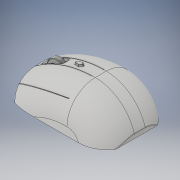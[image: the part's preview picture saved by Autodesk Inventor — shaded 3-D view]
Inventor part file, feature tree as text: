
AUTODESK INVENTOR PART (.ipt)
format: ipt  version: 2017 (Build 210142000, 142)  size: 1,075,200 bytes
history: native  units: in
note: dims shown in document units (in); Inventor stores cm internally (conversion verified against a paired STEP export)
features: sketch x12, extrude x7, other x6, fillet x5, sweep x2, mirror x1
ambient origin geometry x8: Origin, YZ Plane, XZ Plane, XY Plane, X Axis, Y Axis, Z Axis, Center Point
bodies: Solid1 (feature_tree)
feature tree (33):
  extrude  "main body"  Depth=0.1251in
  other  "middle of the mouse workplane"
  fillet  "curve the edges"  Radius=0.0409in
  other  "gap for mouse clicks"
  sweep  "gap made for mouse clicks"
  sweep  "gap for mouse clicks front"
  extrude  "far left gap for mouse clicks"  Depth=0.2314in TaperAngle=0.0deg
  mirror  "mirror mouse clicks for other side"
  extrude  "mouse wheel gap"  Depth=0.1974in
  extrude  "mouse wheel extion for proper width"  Depth=0.0053in
  fillet  "curve proper width for wheel gap"  [1 undecoded]
  other  "mouse wheel revolve plane"
  other  "wheel"
  extrude  "friction points"  Depth=0.0302in
  fillet  "wheel curve edge"  Radius=0.0046in
  other  "batter indicator workplane"
  extrude  "battery indicator cut out"  Depth=0.0199in TaperAngle=0.0deg
  extrude  "power indicator"  Depth=0.0687in
  fillet  "smooth the powe indicator"  Radius=0.0382in
  fillet  "Fillet6"  Radius=0.0043in
  sketch  "Sketch1"  dims[d0=0.3403in d1=0.1251in d2=0.0409in]
  sketch  "Sketch3"  dims[d3=0.014in d4=0.3157in]
  sketch  "Sketch4"  dims[d5=0.0247in d6=0.1333in]
  sketch  "Sketch6"  dims[d7=0.0143in d8=0.2314in d9=0.0in]
  sketch  "Sketch8"  dims[d10=0.097in d13=0.1974in]
  sketch  "Sketch10"  dims[d14=0.0018in d15=0.0053in d16=0.0in d17=0.0in]
  sketch  "Sketch11"  dims[d18=0.0167in d19=0.0302in d20=0.0046in]
  other  "Work Axis1"
  sketch  "Sketch12"  dims[d21=0.0046in d24=0.0199in d25=0.0in]
  sketch  "Sketch13"  dims[d26=0.003in d28=0.0687in d29=0.0382in d30=0.0043in]
  sketch  "Sketch16"  dims[d31=105.0deg]
  sketch  "3D Sketch2"
  sketch  "Sketch18"  dims[d32=105.0deg d33=0.0203in d34=0.0146in d35=0.0199in d36=0.0in d37=0.0636in d38=0.0156in d39=0.0156in d40=0.003in d41=0.0734in d45=0.0169in d46=0.0299in d47=0.0in d48=0.005in d50=0.0019in d51=90.0deg d52=0.0081in d53=0.001in d54=0.0318in d56=90.0deg d62=41.3386in d64=360.0deg d66=0.0163in d67=0.0143in d68=0.0in d69=0.001in d89=105.0deg d90=105.0deg d91=0.002in d93=0.002in d94=0.002in d97=0.0101in d98=0.0in d99=0.001in d103=0.0053in d104=0.0018in d110=0.0583in d113=0.0in d114=0.0in d116=0.1974in d117=0.1974in d118=0.0018in d119=0.0in d120=0.0018in d121=0.005in]
note: 1 required parameter value undecoded (feature->parameter linkage not recoverable at this tier; creation-order binding heuristic only, values carry confidence <= 0.55)
